# Revit family: Connection-Welded Shear Stud-Composite Floor Decking_Temp_c1c4bf35-942a-4010-ae56-a899d25e8be7
name_source: partatom
category: Structural Connections
revit_build: Autodesk Revit 2016 (Build: 20160314_0715(x64)
units: mm (PartAtom-declared; Revit-internal decimal feet)

## family parameters
Cut with Voids When Loaded = No
Enable cutting in views = Yes
Host = Face
Material for Model Behavior = Steel
Shared = No

## types (1)
- 150mm
    CBICode = 3151
    CBIDescription = Composite construction of in situ concrete and permanent formwork
    ComFlor Design Software = http://www.comflor.nz
    ComFlor Technical Resources = http://www.comflor.nz
    Default Elevation = 1219 mm
    Description = Stud shear connector for use with ComFlor® range
    Head = 12 mm  [stored 0.0393701 ft]
    Head Radius = 16 mm  [stored 0.0524934 ft]
    Manufacturer = Supplied by Steel & Tube
    ManufacturerName = Supplied by Steel & Tube
    ManufacturerURL = http://www.steelandtube.co.nz
    Material Standard = AS/NZS 1554.2:2003
    Model = Welded Shear Stud
    SpecificationDescription = ComFlor composite floor system
    SpecificationReference = 3151C
    Stud Length = 150 mm
    Stud Material = Metal
    Stud Radius = 10 mm  [stored 0.0328084 ft]
    Trademark = ComFlor® is a registered trade mark used in Australia and New Zealand under licence from Tata Steel UK Limited.
    Type Comments = G450 Steel
    URL = http://www.comflor.nz
    Uniclass2015Code = Ss_30_12_85_16
    Uniclass2015Title = Composite steel and concrete floor, roof or balcony deck systems
    Uniclass2015Version = 2015

note: [stored X ft] marks values corroborated as IEEE doubles in the binary element streams (Revit-internal decimal feet)

## geometry (parser evidence)
native form markers: Sweep x2
no freeform markers — native parametric forms only
